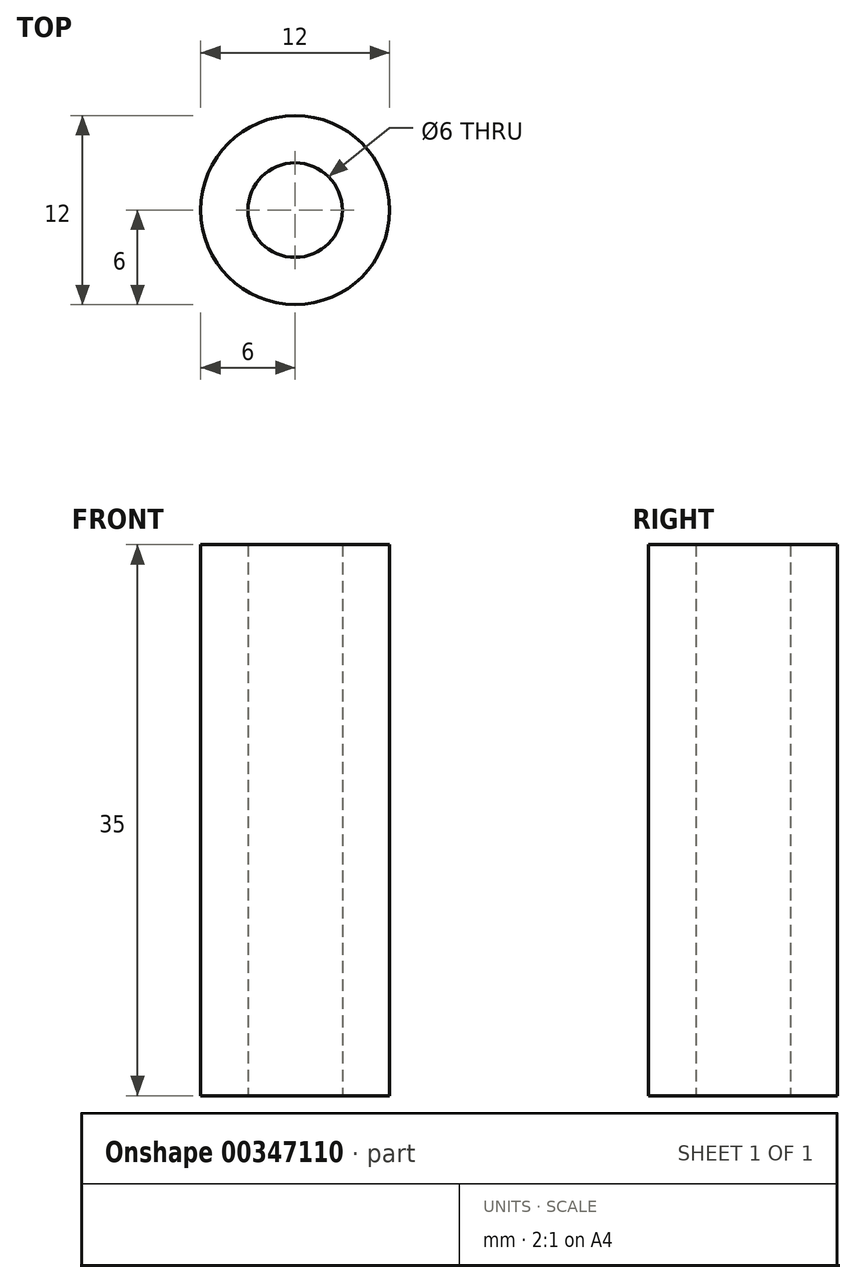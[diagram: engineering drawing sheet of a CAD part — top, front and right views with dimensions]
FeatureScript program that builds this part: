
annotation { "Feature Type Name" : "Feature", "Feature Type Description" : "" }
export const myFeature = defineFeature(function(context is Context, id is Id, definition is map)
    precondition{}
    {
        {
            var Q0;
            Q0=qCreatedBy(makeId("Top.planeOp"),FACE);
            var sketch = newSketch(context, id + "F0", { "sketchPlane" : qUnion([Q0])});
            skCircle(sketch, "E0", {"center": v(0, 0) * mm, "radius": 6 * mm});
            skCircle(sketch, "E1", {"center": v(0, 0) * mm, "radius": 3 * mm});
            skSolve(sketch);
        }
        {
            var Q0;
            Q0=makeQuery(id+"F0.imprint","IMPRINT",FACE,{"disambiguationData":[TD([[makeQuery(id+"F0.imprint","IMPRINT",EDGE,{"derivedFrom":sQuery(id+"F0.wireOp",EDGE,"E0")}),1.0]])]});
            extrude(context, id + "F1", {"entities" : qUnion([Q0]), "depth" : 35 * mm});
        }
    });
